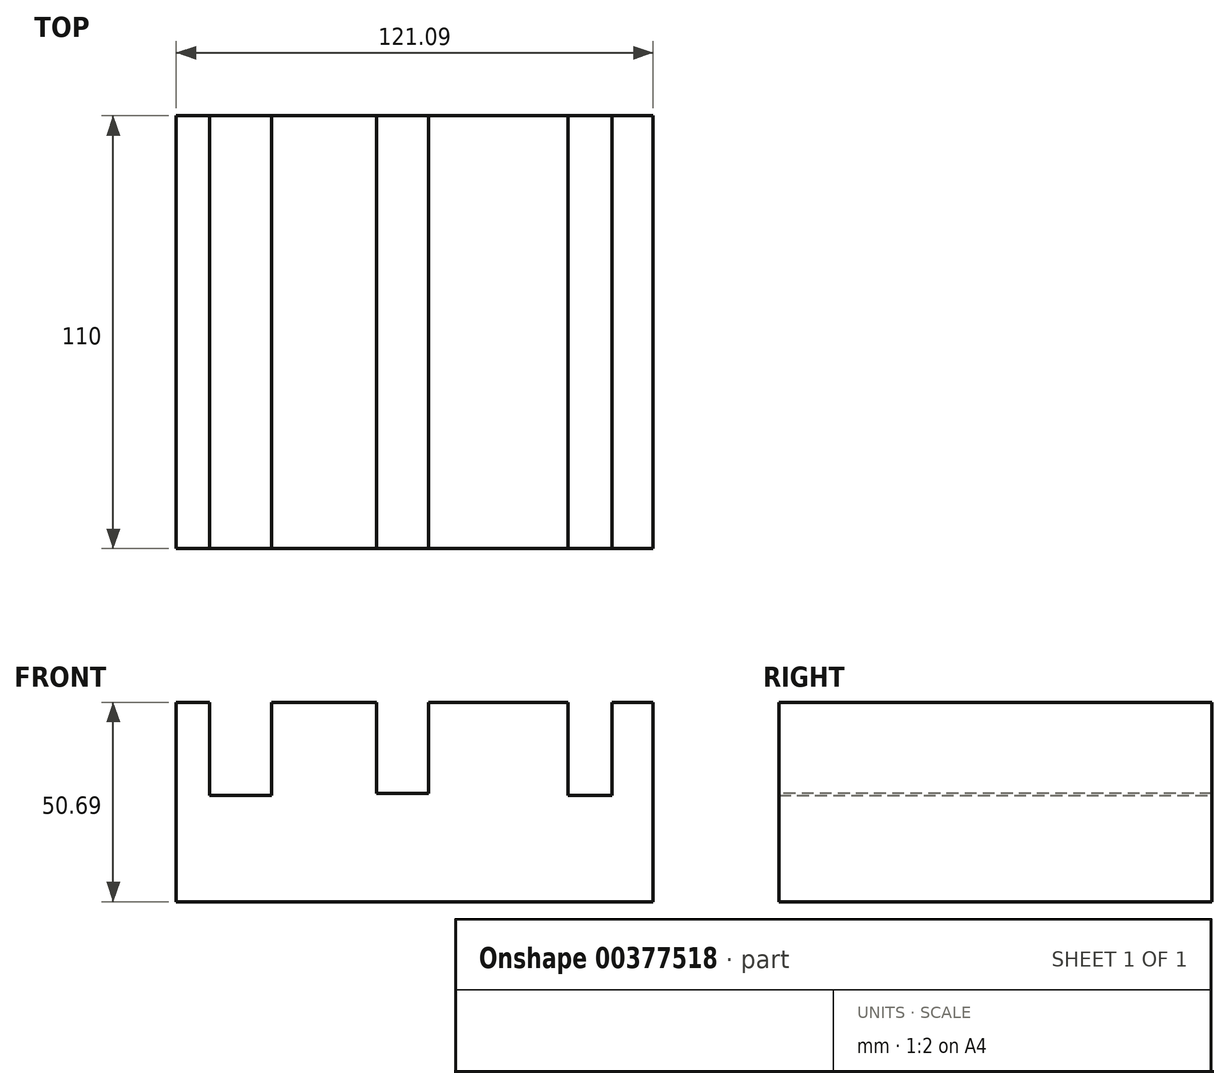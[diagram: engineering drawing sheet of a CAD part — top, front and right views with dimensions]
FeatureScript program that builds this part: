
annotation { "Feature Type Name" : "Feature", "Feature Type Description" : "" }
export const myFeature = defineFeature(function(context is Context, id is Id, definition is map)
    precondition{}
    {
        {
            var Q0;
            Q0=qCreatedBy(makeId("Front.planeOp"),FACE);
            var sketch = newSketch(context, id + "F0", { "sketchPlane" : qUnion([Q0])});
            skLineSegment(sketch, "E0.bottom", {"start": v(-63.33, 0) * mm, "end": v(-47.58, 0) * mm});
            skLineSegment(sketch, "E0.top", {"start": v(-63.33, -23.68) * mm, "end": v(-47.58, -23.68) * mm});
            skLineSegment(sketch, "E0.left", {"start": v(-63.33, 0) * mm, "end": v(-63.33, -23.68) * mm});
            skLineSegment(sketch, "E0.right", {"start": v(-47.58, 0) * mm, "end": v(-47.58, -23.68) * mm});
            skLineSegment(sketch, "E1.bottom", {"start": v(-31.25, 0) * mm, "end": v(-29.68, 0) * mm});
            skLineSegment(sketch, "E1.top", {"start": v(-31.25, -23.68) * mm, "end": v(-29.68, -23.68) * mm});
            skLineSegment(sketch, "E1.left", {"start": v(-31.25, 0) * mm, "end": v(-31.25, -23.68) * mm});
            skLineSegment(sketch, "E1.right", {"start": v(-29.68, 0) * mm, "end": v(-29.68, -23.68) * mm});
            skLineSegment(sketch, "E2.bottom", {"start": v(27.67, 0) * mm, "end": v(38.96, 0) * mm});
            skLineSegment(sketch, "E2.top", {"start": v(27.67, -23.68) * mm, "end": v(38.96, -23.68) * mm});
            skLineSegment(sketch, "E2.left", {"start": v(27.67, 0) * mm, "end": v(27.67, -23.68) * mm});
            skLineSegment(sketch, "E2.right", {"start": v(38.96, 0) * mm, "end": v(38.96, -23.68) * mm});
            skLineSegment(sketch, "E3.bottom", {"start": v(-71.78, 0) * mm, "end": v(49.31, 0) * mm});
            skLineSegment(sketch, "E3.top", {"start": v(-71.78, -50.69) * mm, "end": v(49.31, -50.69) * mm});
            skLineSegment(sketch, "E3.left", {"start": v(-71.78, 0) * mm, "end": v(-71.78, -50.69) * mm});
            skLineSegment(sketch, "E3.right", {"start": v(49.31, 0) * mm, "end": v(49.31, -50.69) * mm});
            skSolve(sketch);
        }
        {
            var Q0;
            Q0=makeQuery(id+"F0.imprint","IMPRINT",FACE,{"disambiguationData":[TD([[makeQuery(id+"F0.imprint","IMPRINT",EDGE,{"derivedFrom":sQuery(id+"F0.wireOp",EDGE,"E1.top")}),1.0]])]});
            var Q1;
            Q1=makeQuery(id+"F0.imprint","IMPRINT",FACE,{"disambiguationData":[TD([[makeQuery(id+"F0.imprint","IMPRINT",EDGE,{"derivedFrom":sQuery(id+"F0.wireOp",EDGE,"E0.top")}),-1.0]])]});
            extrude(context, id + "F1", {"entities" : qUnion([Q0, Q1]), "depth" : 110 * mm});
        }
        {
            var Q0;
            Q0=makeQuery(id+"F1.opExtrude","CAP_FACE",FACE,{"disambiguationData":[OSD([sQuery(id+"F0.wireOp",EDGE,"E0.top"),sQuery(id+"F0.wireOp",EDGE,"E0.left"),sQuery(id+"F0.wireOp",EDGE,"E0.right"),sQuery(id+"F0.wireOp",EDGE,"E2.top"),sQuery(id+"F0.wireOp",EDGE,"E2.left"),sQuery(id+"F0.wireOp",EDGE,"E2.right"),sQuery(id+"F0.wireOp",EDGE,"E3.bottom"),sQuery(id+"F0.wireOp",EDGE,"E3.top"),sQuery(id+"F0.wireOp",EDGE,"E3.left"),sQuery(id+"F0.wireOp",EDGE,"E3.right")])],"isStart":false});
            var sketch = newSketch(context, id + "F2", { "sketchPlane" : qUnion([Q0])});
            skLineSegment(sketch, "E4.bottom", {"start": v(-20.93, 0) * mm, "end": v(-7.7, 0) * mm});
            skLineSegment(sketch, "E4.top", {"start": v(-20.93, -23.13) * mm, "end": v(-7.7, -23.13) * mm});
            skLineSegment(sketch, "E4.left", {"start": v(-20.93, 0) * mm, "end": v(-20.93, -23.13) * mm});
            skLineSegment(sketch, "E4.right", {"start": v(-7.7, 0) * mm, "end": v(-7.7, -23.13) * mm});
            skLineSegment(sketch, "E5.bottom", {"start": v(3.44, 0) * mm, "end": v(14.73, 0) * mm});
            skLineSegment(sketch, "E5.top", {"start": v(3.44, -23.68) * mm, "end": v(14.73, -23.68) * mm});
            skLineSegment(sketch, "E5.left", {"start": v(3.44, 0) * mm, "end": v(3.44, -23.68) * mm});
            skLineSegment(sketch, "E5.right", {"start": v(14.73, 0) * mm, "end": v(14.73, -23.68) * mm});
            skSolve(sketch);
        }
        {
            var Q0;
            Q0=makeQuery(id+"F2.imprint","IMPRINT",FACE,{"disambiguationData":[TD([[makeQuery(id+"F2.imprint","IMPRINT",EDGE,{"derivedFrom":sQuery(id+"F2.wireOp",EDGE,"E4.bottom")}),-1.0]])]});
            extrude(context, id + "F3", {"entities" : qUnion([Q0]), "operationType" : NewBodyOperationType.REMOVE, "oppositeDirection" : true, "depth" : 129 * mm});
        }
    });
